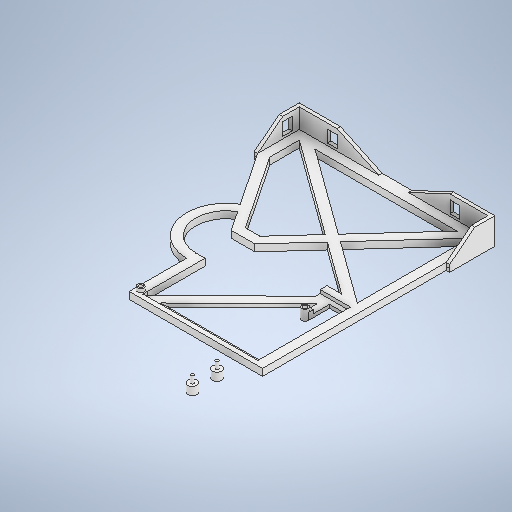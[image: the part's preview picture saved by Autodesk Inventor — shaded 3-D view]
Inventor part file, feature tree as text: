
AUTODESK INVENTOR PART (.ipt)
format: ipt  version: 2025.2 (Build 292293000, 293)  size: 657,920 bytes
history: native  units: mm
features: extrude x17, sketch x5
ambient origin geometry x8: Origin, YZ Plane, XZ Plane, XY Plane, X Axis, Y Axis, Z Axis, Center Point
bodies: Solid1 (feature_tree)
feature tree (22):
  sketch  "Sketch1"  dims[d0=82.0mm d1=54.0mm]
  extrude  "Extrusion1"  Depth=54.0mm
  extrude  "Extrusion2"  Depth=3.0mm
  extrude  "Extrusion3"  Depth=2.9mm
  extrude  "Extrusion4"  Depth=1.5mm TaperAngle=0.0deg
  extrude  "Extrusion5"  Depth=12.24mm
  extrude  "Extrusion6"  Depth=4.2mm
  extrude  "Extrusion10"  Depth=5.2mm
  sketch  "Sketch16"  dims[d6=2.9mm d8=12.5mm]
  extrude  "Extrusion11"  Depth=1.0mm
  extrude  "Extrusion12"  Depth=1.5mm TaperAngle=0.0deg
  extrude  "Extrusion13"  Depth=1.5mm TaperAngle=0.0deg
  extrude  "Extrusion14"  Depth=1.5mm TaperAngle=0.0deg
  extrude  "Extrusion15"  Depth=4.5mm
  extrude  "Extrusion16"  Depth=4.5mm
  extrude  "Extrusion17"  Depth=5.5mm
  extrude  "Extrusion18"  Depth=1.0mm
  extrude  "Extrusion19"  Depth=0.5mm
  extrude  "Extrusion20"  Depth=1.5mm TaperAngle=0.0deg
  sketch  "Sketch2"  dims[d2=44.0mm d5=3.0mm]
  sketch  "Sketch25"  dims[d9=2.9mm d10=1.5mm d11=0.0mm]
  sketch  "Sketch26"  dims[d13=10.0mm d14=12.24mm d16=4.2mm d17=5.2mm d18=1.0mm d19=1.5mm d20=0.0mm d22=1.5mm d23=0.0mm d24=1.5mm d25=0.0mm d26=4.5mm d27=4.5mm d28=5.5mm d29=1.0mm d30=13.825495mm d31=1.5mm d32=0.0mm d34=20.0mm d35=16.44mm d36=18.104mm d37=3.0mm d38=0.0mm d76=1.7mm d78=0.0mm d79=0.0mm d80=4.0mm d81=1.3mm d83=2.0mm d84=0.0mm d85=2.0mm d86=0.0mm d87=5.0mm d88=0.0mm d94=90.0deg d95=90.0deg d96=31.0mm d97=4.0mm d98=4.0mm d103=4.0mm d104=4.0mm d105=1.5mm d106=0.0mm d107=1.5mm d108=0.0mm d110=1.8mm d112=4.0mm d113=7.765622mm d114=1.5mm d115=0.0mm d121=23.473586mm d122=23.650304mm d123=13.528693mm d124=13.140289mm d125=90.0deg d126=9.427875mm d127=7.403962mm d128=4.0mm d129=4.0mm d130=25.52254mm d131=11.748234mm d132=25.0mm d133=51.672948mm d134=4.0mm d135=7.2mm d136=1.5mm d137=1.5mm d138=1.5mm d139=0.0mm d140=2.0mm d141=17.152547mm d142=2.0mm d143=7.942341mm d144=7.0mm d146=1.5mm d147=0.0mm d148=1.5mm d149=0.0mm d150=2.0mm d151=1.5mm d152=0.0mm d154=0.5mm d155=58.0mm d116=0.5mm d117=0.872665mm]
